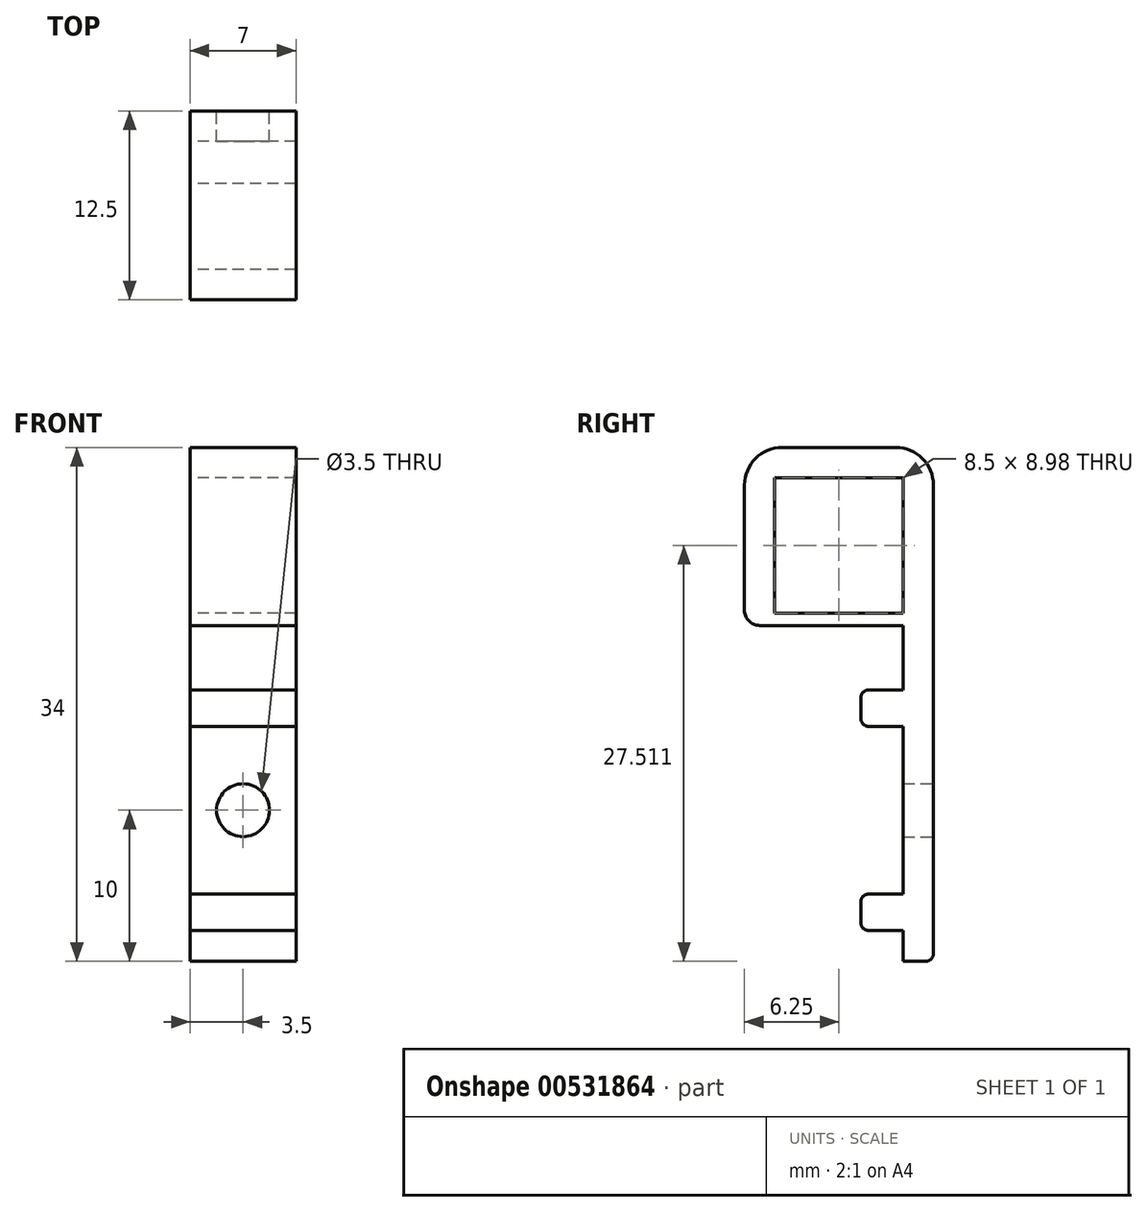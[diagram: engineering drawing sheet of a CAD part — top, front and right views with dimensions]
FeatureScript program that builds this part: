
annotation { "Feature Type Name" : "Feature", "Feature Type Description" : "" }
export const myFeature = defineFeature(function(context is Context, id is Id, definition is map)
    precondition{}
    {
        {
            var Q0;
            Q0=qCreatedBy(makeId("Front.planeOp"),FACE);
            var sketch = newSketch(context, id + "F0", { "sketchPlane" : qUnion([Q0])});
            skLineSegment(sketch, "E0.bottom", {"start": v(0, 0) * mm, "end": v(7, 0) * mm});
            skLineSegment(sketch, "E0.top", {"start": v(0, 20) * mm, "end": v(7, 20) * mm});
            skLineSegment(sketch, "E0.left", {"start": v(0, 0) * mm, "end": v(0, 20) * mm});
            skLineSegment(sketch, "E0.right", {"start": v(7, 0) * mm, "end": v(7, 20) * mm});
            skCircle(sketch, "E1", {"center": v(3.5, 10) * mm, "radius": 1.75 * mm});
            skSolve(sketch);
        }
        {
            var Q0;
            Q0=qSketchRegion(id+"F0",true);
            extrude(context, id + "F1", {"entities" : qUnion([Q0]), "depth" : 2 * mm});
        }
        {
            var Q0;
            Q0=makeQuery(id+"F1.opExtrude","CAP_FACE",FACE,{"disambiguationData":[OSD([sQuery(id+"F0.wireOp",EDGE,"E0.bottom"),sQuery(id+"F0.wireOp",EDGE,"E0.top"),sQuery(id+"F0.wireOp",EDGE,"E0.left"),sQuery(id+"F0.wireOp",EDGE,"E0.right"),sQuery(id+"F0.wireOp",EDGE,"E1")])],"isStart":false});
            var sketch = newSketch(context, id + "F2", { "sketchPlane" : qUnion([Q0])});
            skLineSegment(sketch, "E2", {"start": v(3.5, 10) * mm, "end": v(3.5, 3.25) * mm});
            skLineSegment(sketch, "E3", {"start": v(3.5, 10) * mm, "end": v(3.5, 16.75) * mm});
            skLineSegment(sketch, "E4.bottom", {"start": v(7, 15.55) * mm, "end": v(0, 15.55) * mm});
            skLineSegment(sketch, "E4.top", {"start": v(7, 17.95) * mm, "end": v(0, 17.95) * mm});
            skLineSegment(sketch, "E4.left", {"start": v(7, 15.55) * mm, "end": v(7, 17.95) * mm});
            skLineSegment(sketch, "E4.right", {"start": v(0, 15.55) * mm, "end": v(0, 17.95) * mm});
            skPoint(sketch, "E4.middle", {"position": v(3.5, 16.75) * mm});
            skLineSegment(sketch, "E5.bottom", {"start": v(7, 4.45) * mm, "end": v(0, 4.45) * mm});
            skLineSegment(sketch, "E5.top", {"start": v(7, 2.05) * mm, "end": v(0, 2.05) * mm});
            skLineSegment(sketch, "E5.left", {"start": v(7, 4.45) * mm, "end": v(7, 2.05) * mm});
            skLineSegment(sketch, "E5.right", {"start": v(0, 4.45) * mm, "end": v(0, 2.05) * mm});
            skPoint(sketch, "E5.middle", {"position": v(3.5, 3.25) * mm});
            skSolve(sketch);
        }
        {
            var Q0;
            Q0=qSketchRegion(id+"F2",true);
            extrude(context, id + "F3", {"entities" : qUnion([Q0]), "operationType" : NewBodyOperationType.ADD, "depth" : 2.8 * mm});
        }
        {
            var Q0;
            Q0=makeQuery(id+"F3.opExtrude","CAP_EDGE",EDGE,{"disambiguationData":[OSD([sQuery(id+"F2.wireOp",EDGE,"E5.top")])],"isStart":false});
            var Q1;
            Q1=makeQuery(id+"F3.opExtrude","CAP_EDGE",EDGE,{"disambiguationData":[OSD([sQuery(id+"F2.wireOp",EDGE,"E5.bottom")])],"isStart":false});
            var Q2;
            Q2=makeQuery(id+"F3.opExtrude","CAP_EDGE",EDGE,{"disambiguationData":[OSD([sQuery(id+"F2.wireOp",EDGE,"E4.bottom")])],"isStart":false});
            var Q3;
            Q3=makeQuery(id+"F3.opExtrude","CAP_EDGE",EDGE,{"disambiguationData":[OSD([sQuery(id+"F2.wireOp",EDGE,"E4.top")])],"isStart":false});
            fillet(context, id + "F4", {"entities" : qUnion([Q0, Q1, Q2, Q3]), "radius" : 0.5 * mm, "tangentPropagation" : true, "allowEdgeOverflow" : false});
        }
        {
            var Q0;
            Q0=makeQuery(id+"F1.opExtrude","CAP_EDGE",EDGE,{"disambiguationData":[OSD([sQuery(id+"F0.wireOp",EDGE,"E0.bottom")])],"isStart":true});
            fillet(context, id + "F5", {"entities" : qUnion([Q0]), "radius" : 0.5 * mm, "tangentPropagation" : true, "allowEdgeOverflow" : false});
        }
        {
            var Q0;
            Q0=makeQuery(id+"F3.boolean.opBoolean","MERGE",FACE,{"derivedFrom":[makeQuery(id+"F1.opExtrude","SWEPT_FACE",FACE,{"disambiguationData":[OSD([sQuery(id+"F0.wireOp",EDGE,"E0.left")])]}),makeQuery(id+"F3.opExtrude","SWEPT_FACE",FACE,{"disambiguationData":[OSD([sQuery(id+"F2.wireOp",EDGE,"E4.right")])]}),makeQuery(id+"F3.opExtrude","SWEPT_FACE",FACE,{"disambiguationData":[OSD([sQuery(id+"F2.wireOp",EDGE,"E5.right")])]})]});
            var sketch = newSketch(context, id + "F6", { "sketchPlane" : qUnion([Q0])});
            skLineSegment(sketch, "E6", {"start": v(2, 20) * mm, "end": v(2, 22.62) * mm});
            skLineSegment(sketch, "E7", {"start": v(2, 32) * mm, "end": v(10.5, 32) * mm});
            skLineSegment(sketch, "E8", {"start": v(2, 20) * mm, "end": v(0, 20) * mm});
            skLineSegment(sketch, "E9", {"start": v(0, 20) * mm, "end": v(0, 34) * mm});
            skLineSegment(sketch, "E10", {"start": v(0, 34) * mm, "end": v(12.5, 34) * mm});
            skLineSegment(sketch, "E11", {"start": v(2, 20) * mm, "end": v(2, 22.22) * mm});
            skLineSegment(sketch, "E12", {"start": v(10.5, 32) * mm, "end": v(10.5, 23.02) * mm});
            skLineSegment(sketch, "E13.bottom", {"start": v(2, 23.02) * mm, "end": v(10.5, 23.02) * mm});
            skLineSegment(sketch, "E13.top", {"start": v(2, 22.22) * mm, "end": v(11.03, 22.22) * mm});
            skPoint(sketch, "E13.middle", {"position": v(6.25, 22.62) * mm});
            skLineSegment(sketch, "E14", {"start": v(12.5, 34) * mm, "end": v(12.5, 22.22) * mm});
            skLineSegment(sketch, "E15", {"start": v(12.5, 22.22) * mm, "end": v(11.03, 22.22) * mm});
            skPoint(sketch, "E16.orphan", {"position": v(11.03, 23.02) * mm});
            skPoint(sketch, "E17.orphan", {"position": v(10.5, 22.62) * mm});
            skPoint(sketch, "E13.left.end.orphan", {"position": v(1.47, 22.22) * mm});
            skPoint(sketch, "E18.orphan", {"position": v(1.47, 23.02) * mm});
            skPoint(sketch, "E19.orphan", {"position": v(2, 22.62) * mm});
            skLineSegment(sketch, "E20.trimOffspring", {"start": v(2, 23.02) * mm, "end": v(2, 32) * mm});
            skSolve(sketch);
        }
        {
            var Q0;
            Q0=qSketchRegion(id+"F6",true);
            var Q1;
            Q1=makeQuery(id+"F3.boolean.opBoolean","MERGE",FACE,{"derivedFrom":[makeQuery(id+"F1.opExtrude","SWEPT_FACE",FACE,{"disambiguationData":[OSD([sQuery(id+"F0.wireOp",EDGE,"E0.right")])]}),makeQuery(id+"F3.opExtrude","SWEPT_FACE",FACE,{"disambiguationData":[OSD([sQuery(id+"F2.wireOp",EDGE,"E4.left")])]}),makeQuery(id+"F3.opExtrude","SWEPT_FACE",FACE,{"disambiguationData":[OSD([sQuery(id+"F2.wireOp",EDGE,"E5.left")])]})]});
            extrude(context, id + "F7", {"entities" : qUnion([Q0]), "operationType" : NewBodyOperationType.ADD, "endBound" : BoundingType.UP_TO_SURFACE, "oppositeDirection" : true, "endBoundEntityFace" : qUnion([Q1]), "depth" : 25 * mm});
        }
        {
            var Q0;
            Q0=makeQuery(id+"F7.opExtrude","SWEPT_EDGE",EDGE,{"disambiguationData":[OSD([sQuery(id+"F6.wireOp",EDGE,"E10"),sQuery(id+"F6.wireOp",EDGE,"E14")])]});
            var Q1;
            Q1=makeQuery(id+"F7.opExtrude","SWEPT_EDGE",EDGE,{"disambiguationData":[OSD([sQuery(id+"F6.wireOp",EDGE,"E9"),sQuery(id+"F6.wireOp",EDGE,"E10")])]});
            fillet(context, id + "F8", {"entities" : qUnion([Q0, Q1]), "radius" : 2.5 * mm, "tangentPropagation" : true, "allowEdgeOverflow" : false});
        }
        {
            var Q0;
            Q0=makeQuery(id+"F7.opExtrude","SWEPT_EDGE",EDGE,{"disambiguationData":[OSD([sQuery(id+"F6.wireOp",EDGE,"E14"),sQuery(id+"F6.wireOp",EDGE,"E15")])]});
            fillet(context, id + "F9", {"entities" : qUnion([Q0]), "radius" : 1 * mm, "tangentPropagation" : true, "allowEdgeOverflow" : false});
        }
    });
